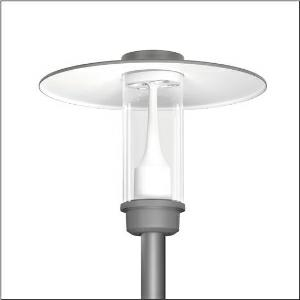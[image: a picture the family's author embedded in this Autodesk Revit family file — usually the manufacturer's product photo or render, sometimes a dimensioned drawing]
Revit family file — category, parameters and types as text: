
# Revit family: litepole_2_iq___st1_2a_5xa5425ef14h_fad6
name_source: partatom
category: Lighting Fixtures
units: mm (PartAtom-declared; Revit-internal decimal feet)

## family parameters
Cut with Voids When Loaded = No
Host = Face
Light Source = No
Part Type = Normal
Room Calculation Point = No
Round Connector Dimension = Use Diameter
Shared = No

## types (1)
- --- (1 x LED, 1550 lm, 10.5 W, 3000K)
    Apparent Load = 11 VA
    CIE Flux Codes = 22 60 92 98 100
    Color Rendering = 70
    Color Temperature = 3000K
    Default Elevation = 1800 mm
    Description = Litepole 2 iQ, mast luminaire, Module 540 iQ-SR, primary light control with 3 zone facetted reflector, of plastic, silver coated, highly specular, structured, primary optical cover: cover, of PMMA, transparent, light distribution: ST1.2a, light emission: direct distribution, primary light characteristic: asymmetric, installation type: post-top, LED, High Power LED, rated luminous flux: 1.550lm, luminous efficacy: 148lm/W, light colour: 730, colour temperature: 3000K, control gear: iQ Street-Remote, control: Auto-Match, Temp-Guard, Lumen-Switch, Night-Set, Smart-Wire, Light-Fading, Desk-Remote (wireless, voltage-free reading and setting of iQ features in the workshop via application-optimized NFC function/RFID function), optimised constant luminous flux control (CLO 2.0), Street-Remote, pre-setting: logarithmic dimming characteristic, with terminal, 6-pole, max. 2.5mm², mains connection: 230..240V, AC, 50/60Hz, start of lifetime: 11W, end of service life: 11W, reduction: 5W, luminaire housing, upper part, of aluminium, coated, Siteco® metallic grey (DB 702S), diameter: 750mm, height: 590mm, spigot size: d x l = 76 x 70mm (post-top) | with reducer (optional accessory) 60 x 70mm, mounting height: 3..5m, post-top mast mounting element, of diecast aluminium, coated, Siteco® metallic grey (DB 702S), Module 540 iQ-SR, traffic white (RAL 9016), equipment: standard, protection rating (complete): IP65, insulation class (complete): insulation class II (safety insulation), certification: CE, ENEC, VDE, packaging unit: 1 piece

Light Distribution: ST1.2a
    Height = 590 mm
    Lamp = 1 x LED
    Lamp Light Flux = 1550 lm
    Lamp Power = 10.5 W
    Lamp count = 1
    Length = 750 mm
    Luminous efficacy = 148 lm/W
    Manufacturer = Siteco
    ModVariant = No
    Model = 5XA5425EF14H
    Number of Poles = 1
    OnlyDefault = Yes
    Power Factor = 1
    Product Name = Litepole 2 iQ | ST1.2a
    Product group = mast luminaire | pylon top
    ProductGroupID = 6100
    Protection Class = Protection class II
    Protection Degree = IP 65
    RLX_Detail_Level = 1
    RLX_Emergency_Light_Flux = 0 lm
    RLX_Emergency_Type = 0
    RLX_Emergency_Type_DB = No
    RlxData = <blob elided: 63537 chars, md5=b1491171>
    Socket = socket
    Standby Power = 0 W
    System Light Flux = 1550 lm
    System Power = 11 W
    Type Comments = factory setting: luminous flux: 100 % | dim-lin: 254 | 419 mA
    Type Image = l_1006518.jpg
    URL = http://relux.com
    VarID = @adj_192642
    Voltage = 0 V
    Weight = 0.00 kg
    Width = 0 mm  [stored 0 ft]

note: [stored X ft] marks values corroborated as IEEE doubles in the binary element streams (Revit-internal decimal feet)

## geometry (parser evidence)
native form markers: Blend x4, Sweep x10
no freeform markers — native parametric forms only
